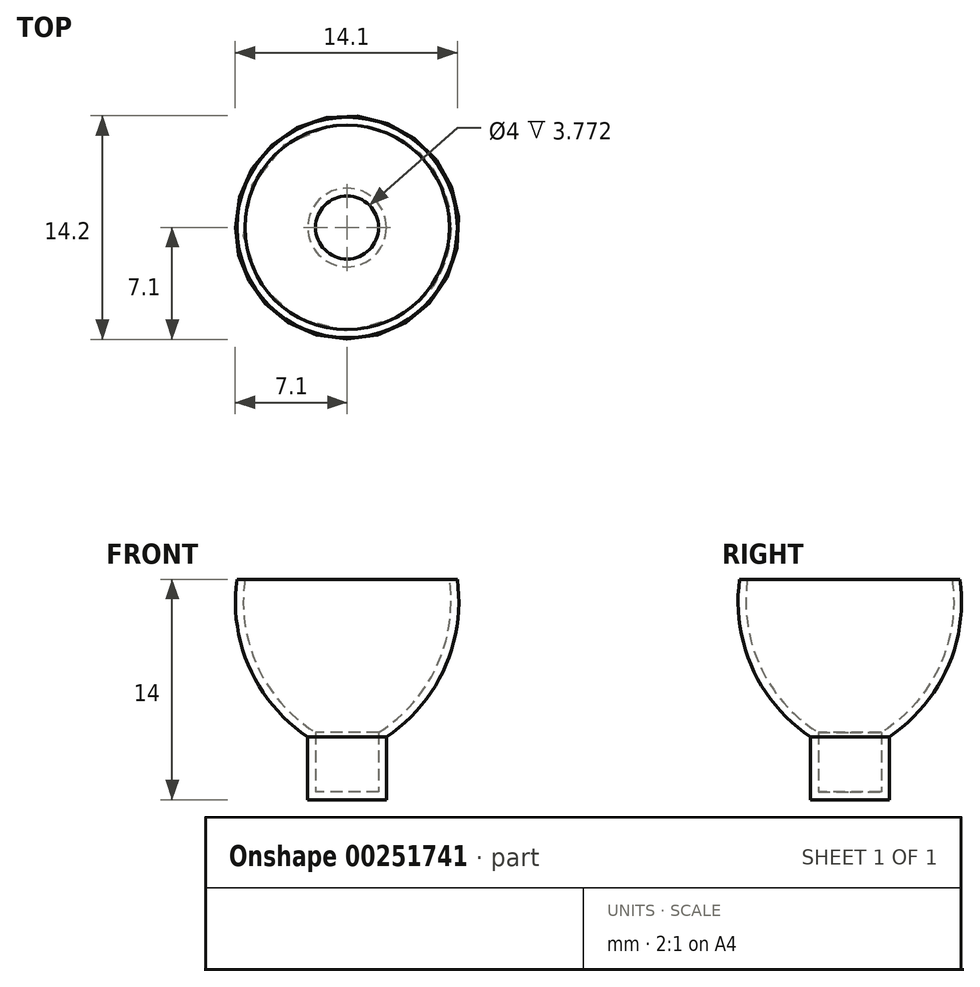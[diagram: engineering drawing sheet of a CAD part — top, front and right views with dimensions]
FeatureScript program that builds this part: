
annotation { "Feature Type Name" : "Feature", "Feature Type Description" : "" }
export const myFeature = defineFeature(function(context is Context, id is Id, definition is map)
    precondition{}
    {
        {
            var Q0;
            Q0=qCreatedBy(makeId("Front.planeOp"),FACE);
            var sketch = newSketch(context, id + "F0", { "sketchPlane" : qUnion([Q0])});
            skLineSegment(sketch, "E0", {"start": v(0, 4) * mm, "end": v(2.5, 4) * mm});
            skLineSegment(sketch, "E1", {"start": v(2.5, 4) * mm, "end": v(2.5, 0) * mm});
            skLineSegment(sketch, "E2", {"start": v(2.5, 0) * mm, "end": v(0, 0) * mm});
            skLineSegment(sketch, "E3", {"start": v(0, 0) * mm, "end": v(0, 4) * mm});
            skArc(sketch, "E4", {"start": v(2.5, 4) * mm, "mid": v(6.19, 8.35) * mm, "end": v(7, 14) * mm});
            skLineSegment(sketch, "E5", {"start": v(7, 14) * mm, "end": v(0, 14) * mm});
            skLineSegment(sketch, "E6", {"start": v(0, 14) * mm, "end": v(0, 4) * mm});
            skSolve(sketch);
        }
        {
            var Q0;
            Q0 = qSketchRegion(id + "F0", true);
            var Q1;
            Q1=sQuery(id+"F0.wireOp",EDGE,"E3");
            revolve(context, id + "F1", {"entities" : qUnion([Q0]), "axis" : qUnion([Q1]), "revolveType" : RevolveType.FULL});
        }
        {
            var Q0;
            Q0=makeQuery(id+"F1.opRevolve","SWEPT_FACE",FACE,{"disambiguationData":[OSD([sQuery(id+"F0.wireOp",EDGE,"E5")])]});
            shell(context, id + "F2", {"entities" : qUnion([Q0]), "thickness" : .5 * mm});
        }
    });
